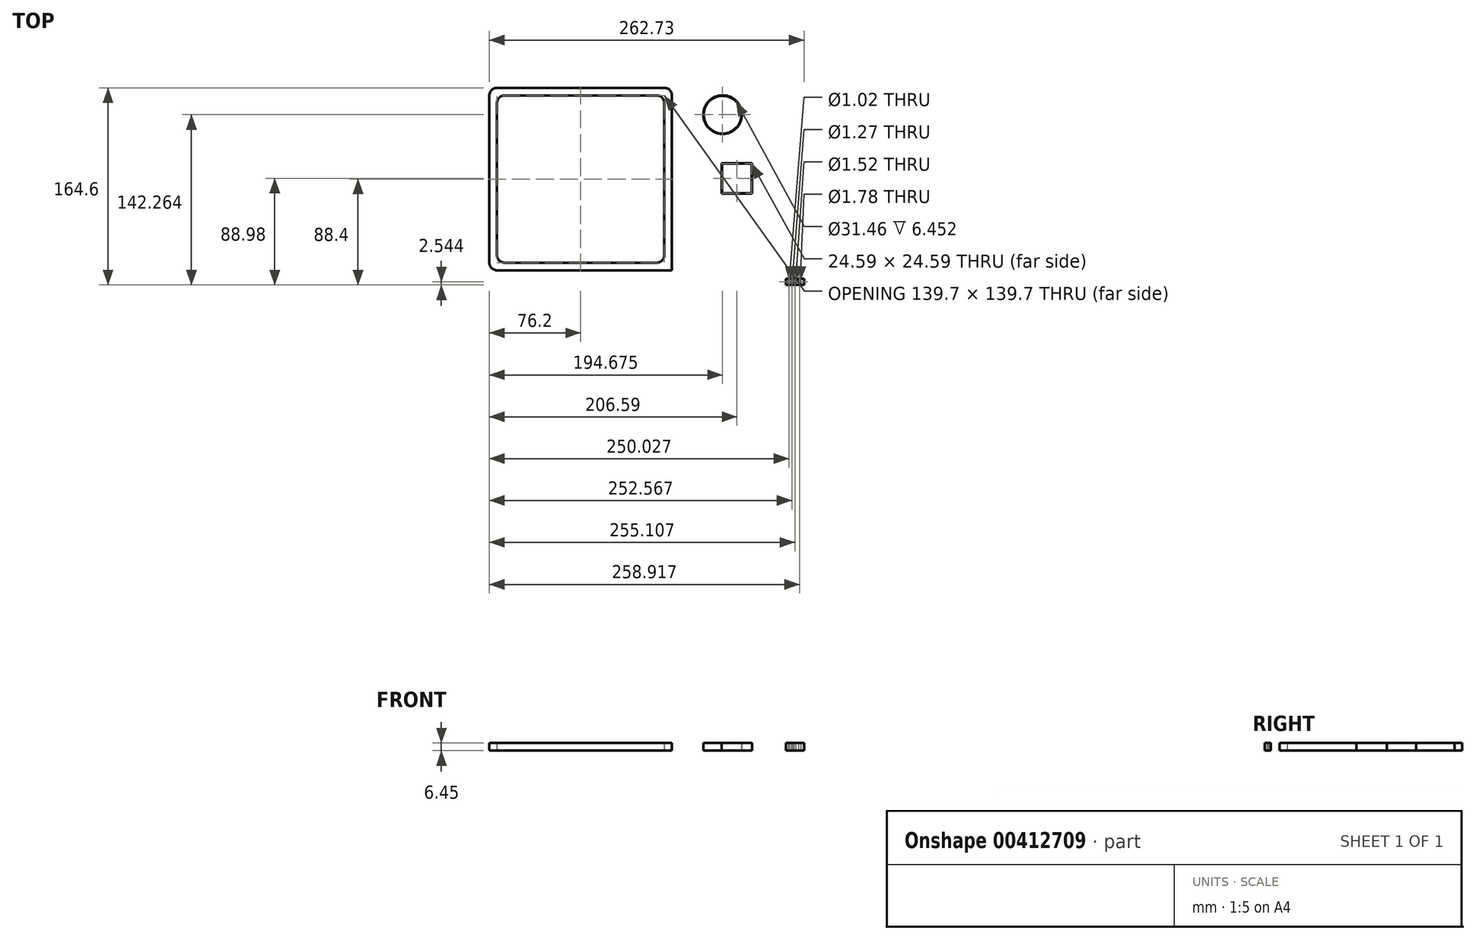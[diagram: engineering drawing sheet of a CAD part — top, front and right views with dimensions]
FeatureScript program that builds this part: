
annotation { "Feature Type Name" : "Feature", "Feature Type Description" : "" }
export const myFeature = defineFeature(function(context is Context, id is Id, definition is map)
    precondition{}
    {
        {
            var Q0;
            Q0=qCreatedBy(makeId("Top.planeOp"),FACE);
            var sketch = newSketch(context, id + "F0", { "sketchPlane" : qUnion([Q0])});
            skLineSegment(sketch, "E0.bottom", {"start": v(-69.85, 76.2) * mm, "end": v(69.85, 76.2) * mm});
            skLineSegment(sketch, "E0.top", {"start": v(-69.85, -76.2) * mm, "end": v(76.2, -76.2) * mm});
            skLineSegment(sketch, "E0.left", {"start": v(-76.2, 69.85) * mm, "end": v(-76.2, -69.85) * mm});
            skLineSegment(sketch, "E0.right", {"start": v(76.2, 69.85) * mm, "end": v(76.2, -76.2) * mm});
            skPoint(sketch, "E1.visualSharp", {"position": v(-76.2, 76.2) * mm});
            skArc(sketch, "E1.filletArc", {"start": v(-69.85, 76.2) * mm, "mid": v(-74.34, 74.34) * mm, "end": v(-76.2, 69.85) * mm});
            skPoint(sketch, "E2.visualSharp", {"position": v(76.2, 76.2) * mm});
            skArc(sketch, "E2.filletArc", {"start": v(76.2, 69.85) * mm, "mid": v(74.34, 74.34) * mm, "end": v(69.85, 76.2) * mm});
            skPoint(sketch, "E3.visualSharp", {"position": v(-76.2, -76.2) * mm});
            skArc(sketch, "E3.filletArc", {"start": v(-76.2, -69.85) * mm, "mid": v(-74.34, -74.34) * mm, "end": v(-69.85, -76.2) * mm});
            skLineSegment(sketch, "E4.bottom", {"start": v(-63.5, 69.85) * mm, "end": v(63.5, 69.85) * mm});
            skLineSegment(sketch, "E4.top", {"start": v(-63.5, -69.85) * mm, "end": v(63.5, -69.85) * mm});
            skLineSegment(sketch, "E4.left", {"start": v(-69.85, 63.5) * mm, "end": v(-69.85, -63.5) * mm});
            skLineSegment(sketch, "E4.right", {"start": v(69.85, 63.5) * mm, "end": v(69.85, -63.5) * mm});
            skArc(sketch, "E5.filletArc", {"start": v(-69.85, -63.5) * mm, "mid": v(-68, -68) * mm, "end": v(-63.5, -69.85) * mm});
            skArc(sketch, "E6.filletArc", {"start": v(-63.5, 69.85) * mm, "mid": v(-68, 68) * mm, "end": v(-69.85, 63.5) * mm});
            skArc(sketch, "E7.filletArc", {"start": v(69.85, 63.5) * mm, "mid": v(68, 68) * mm, "end": v(63.5, 69.85) * mm});
            skPoint(sketch, "E8.visualSharp", {"position": v(69.85, -69.85) * mm});
            skArc(sketch, "E8.filletArc", {"start": v(63.5, -69.85) * mm, "mid": v(68, -68) * mm, "end": v(69.85, -63.5) * mm});
            skLineSegment(sketch, "E9.bottom", {"start": v(117.7, 13.28) * mm, "end": v(143.1, 13.28) * mm});
            skLineSegment(sketch, "E9.top", {"start": v(117.7, -12.12) * mm, "end": v(143.1, -12.12) * mm});
            skLineSegment(sketch, "E9.left", {"start": v(117.7, 13.28) * mm, "end": v(117.7, -12.12) * mm});
            skLineSegment(sketch, "E9.right", {"start": v(143.1, 13.28) * mm, "end": v(143.1, -12.12) * mm});
            skLineSegment(sketch, "E10.0", {"start": v(118.1, -11.71) * mm, "end": v(142.68, -11.71) * mm});
            skLineSegment(sketch, "E11.0", {"start": v(118.1, 12.87) * mm, "end": v(118.1, -11.71) * mm});
            skLineSegment(sketch, "E12.0", {"start": v(118.1, 12.87) * mm, "end": v(142.68, 12.87) * mm});
            skLineSegment(sketch, "E13.0", {"start": v(142.68, 12.87) * mm, "end": v(142.68, -11.71) * mm});
            skCircle(sketch, "E14", {"center": v(118.48, 53.86) * mm, "radius": 16.13 * mm});
            skCircle(sketch, "E15.0", {"center": v(118.48, 53.86) * mm, "radius": 15.73 * mm});
            skLineSegment(sketch, "E16.bottom", {"start": v(171.29, -83.32) * mm, "end": v(186.53, -83.32) * mm});
            skLineSegment(sketch, "E16.top", {"start": v(171.29, -88.4) * mm, "end": v(186.53, -88.4) * mm});
            skLineSegment(sketch, "E16.left", {"start": v(171.29, -83.32) * mm, "end": v(171.29, -88.4) * mm});
            skLineSegment(sketch, "E16.right", {"start": v(186.53, -83.32) * mm, "end": v(186.53, -88.4) * mm});
            skCircle(sketch, "E17", {"center": v(173.83, -85.86) * mm, "radius": 0.5 * mm});
            skPoint(sketch, "E17.centerSnap0", {"position": v(171.29, -85.86) * mm});
            skCircle(sketch, "E18", {"center": v(176.37, -85.86) * mm, "radius": 0.64 * mm});
            skCircle(sketch, "E19", {"center": v(178.9, -85.86) * mm, "radius": 0.76 * mm});
            skCircle(sketch, "E20", {"center": v(182.72, -85.86) * mm, "radius": 0.89 * mm});
            skSolve(sketch);
        }
        {
            var Q0;
            Q0=makeQuery(id+"F0.imprint","IMPRINT",FACE,{"disambiguationData":[TD([[makeQuery(id+"F0.imprint","IMPRINT",EDGE,{"derivedFrom":sQuery(id+"F0.wireOp",EDGE,"E0.bottom")}),-1.0]])]});
            extrude(context, id + "F1", {"entities" : qUnion([Q0]), "depth" : 6.35 * mm});
        }
        {
            var Q0;
            Q0=makeQuery(id+"F0.imprint","IMPRINT",FACE,{"disambiguationData":[TD([[makeQuery(id+"F0.imprint","IMPRINT",EDGE,{"derivedFrom":sQuery(id+"F0.wireOp",EDGE,"E9.bottom")}),-1.0]])]});
            extrude(context, id + "F2", {"entities" : qUnion([Q0]), "depth" : 6.35 * mm});
        }
        {
            var Q0;
            Q0=makeQuery(id+"F0.imprint","IMPRINT",FACE,{"disambiguationData":[TD([[makeQuery(id+"F0.imprint","IMPRINT",EDGE,{"derivedFrom":sQuery(id+"F0.wireOp",EDGE,"E14")}),1.0]])]});
            extrude(context, id + "F3", {"entities" : qUnion([Q0]), "depth" : 6.45 * mm});
        }
        {
            var Q0;
            Q0=makeQuery(id+"F0.imprint","IMPRINT",FACE,{"disambiguationData":[TD([[makeQuery(id+"F0.imprint","IMPRINT",EDGE,{"derivedFrom":sQuery(id+"F0.wireOp",EDGE,"E16.bottom")}),-1.0]])]});
            extrude(context, id + "F4", {"entities" : qUnion([Q0]), "depth" : 6.35 * mm, "offsetDistance" : 25.4 * mm});
        }
    });
